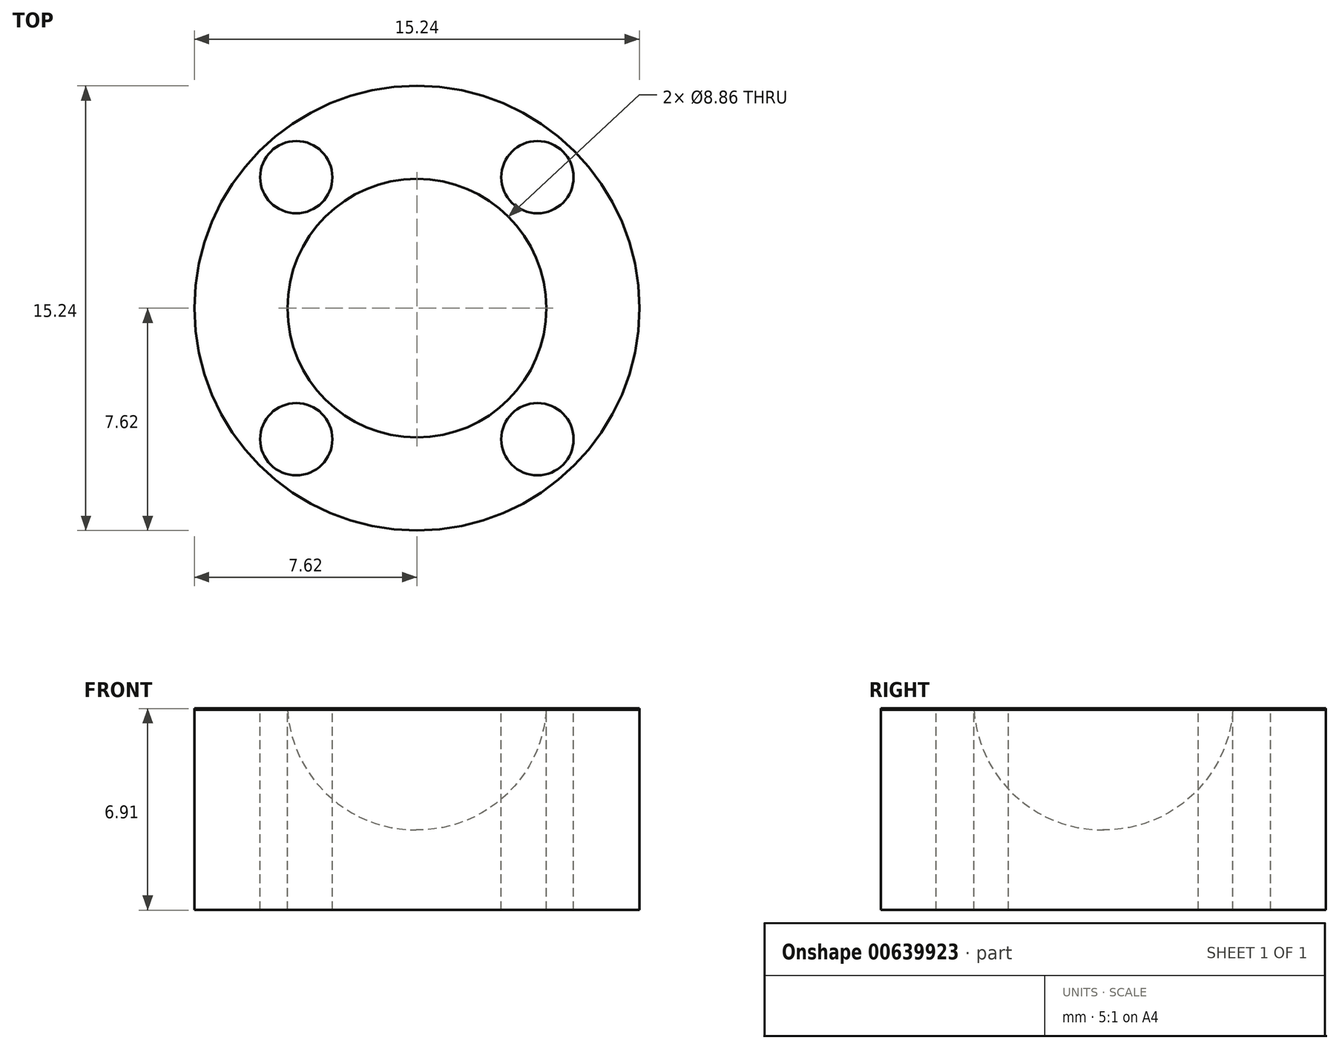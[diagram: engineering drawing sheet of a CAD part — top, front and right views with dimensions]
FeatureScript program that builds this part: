
annotation { "Feature Type Name" : "Feature", "Feature Type Description" : "" }
export const myFeature = defineFeature(function(context is Context, id is Id, definition is map)
    precondition{}
    {
        {
            var Q0;
            Q0=qCreatedBy(makeId("Top.planeOp"),FACE);
            var sketch = newSketch(context, id + "F0", { "sketchPlane" : qUnion([Q0])});
            skCircle(sketch, "E0", {"center": v(0, 0) * mm, "radius": 7.62 * mm});
            skCircle(sketch, "E1", {"center": v(-4.13, -4.5) * mm, "radius": 1.24 * mm});
            skCircle(sketch, "E2.MirrorC", {"center": v(4.13, -4.5) * mm, "radius": 1.24 * mm});
            skCircle(sketch, "E3.MirrorC", {"center": v(-4.13, 4.5) * mm, "radius": 1.24 * mm});
            skCircle(sketch, "E4.MirrorC", {"center": v(4.13, 4.5) * mm, "radius": 1.24 * mm});
            skCircle(sketch, "E5", {"center": v(0, 0) * mm, "radius": 4.43 * mm});
            skSolve(sketch);
        }
        {
            var Q0;
            Q0=makeQuery(id+"F0.imprint","IMPRINT",FACE,{"disambiguationData":[TD([[makeQuery(id+"F0.imprint","IMPRINT",EDGE,{"derivedFrom":sQuery(id+"F0.wireOp",EDGE,"E3.MirrorC")}),-1.0]])]});
            var Q1;
            Q1=makeQuery(id+"F0.imprint","IMPRINT",FACE,{"disambiguationData":[TD([[makeQuery(id+"F0.imprint","IMPRINT",EDGE,{"derivedFrom":sQuery(id+"F0.wireOp",EDGE,"E1")}),1.0]])]});
            var Q2;
            Q2=makeQuery(id+"F0.imprint","IMPRINT",FACE,{"disambiguationData":[TD([[makeQuery(id+"F0.imprint","IMPRINT",EDGE,{"derivedFrom":sQuery(id+"F0.wireOp",EDGE,"E2.MirrorC")}),-1.0]])]});
            var Q3;
            Q3=makeQuery(id+"F0.imprint","IMPRINT",FACE,{"disambiguationData":[TD([[makeQuery(id+"F0.imprint","IMPRINT",EDGE,{"derivedFrom":sQuery(id+"F0.wireOp",EDGE,"E4.MirrorC")}),1.0]])]});
            extrude(context, id + "F1", {"entities" : qUnion([Q0, Q1, Q2, Q3]), "oppositeDirection" : true, "depth" : 6.86 * mm, "offsetDistance" : 25.4 * mm});
        }
        {
            var Q0;
            Q0=makeQuery(id+"F0.imprint","IMPRINT",FACE,{"disambiguationData":[TD([[makeQuery(id+"F0.imprint","IMPRINT",EDGE,{"derivedFrom":sQuery(id+"F0.wireOp",EDGE,"E5")}),1.0]])]});
            extrude(context, id + "F2", {"entities" : qUnion([Q0]), "oppositeDirection" : true, "depth" : 4.11 * mm, "offsetDistance" : 25.4 * mm});
        }
        {
            var Q0;
            Q0=makeQuery(id+"F2.opExtrude","CAP_EDGE",EDGE,{"disambiguationData":[OSD([sQuery(id+"F0.wireOp",EDGE,"E5")])],"isStart":false});
            fillet(context, id + "F3", {"entities" : qUnion([Q0]), "radius" : 4.42 * mm, "tangentPropagation" : true, "allowEdgeOverflow" : false});
        }
        {
            var Q0;
            Q0=makeQuery(id+"F0.imprint","IMPRINT",FACE,{"disambiguationData":[TD([[makeQuery(id+"F0.imprint","IMPRINT",EDGE,{"derivedFrom":sQuery(id+"F0.wireOp",EDGE,"E0")}),1.0]])]});
            extrude(context, id + "F4", {"entities" : qUnion([Q0]), "depth" : 0.05 * mm, "offsetDistance" : 25.4 * mm});
        }
    });
